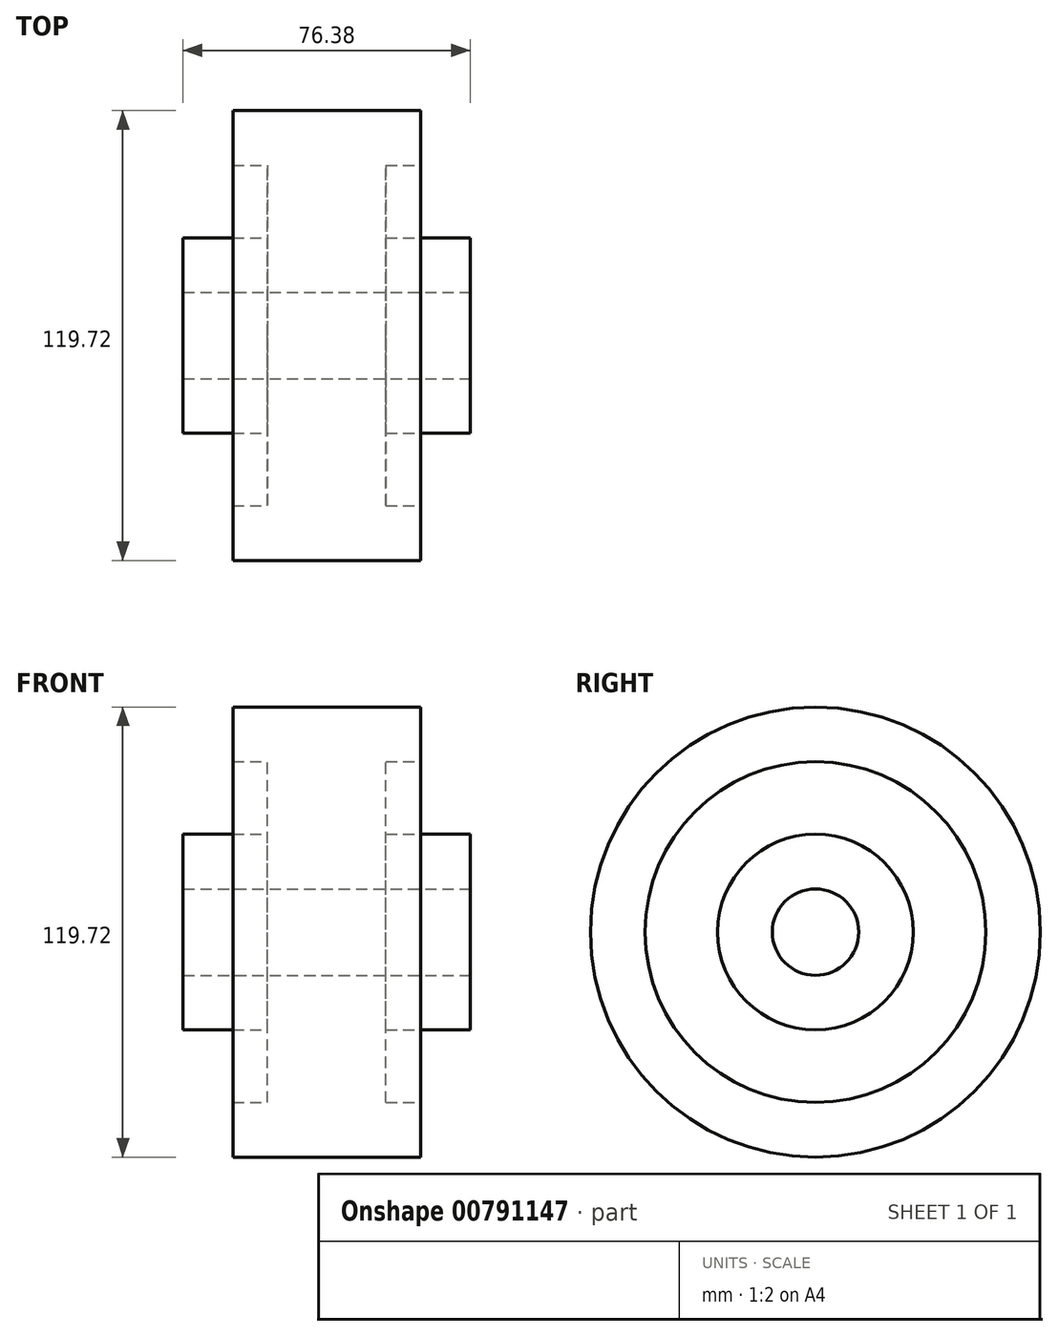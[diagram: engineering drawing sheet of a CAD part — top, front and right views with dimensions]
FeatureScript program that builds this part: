
annotation { "Feature Type Name" : "Feature", "Feature Type Description" : "" }
export const myFeature = defineFeature(function(context is Context, id is Id, definition is map)
    precondition{}
    {
        {
            var Q0;
            Q0=qCreatedBy(makeId("Front.planeOp"),FACE);
            var sketch = newSketch(context, id + "F0", { "sketchPlane" : qUnion([Q0])});
            skLineSegment(sketch, "E0", {"start": v(0, 0) * mm, "end": v(54.83, 0) * mm, "construction": true});
            skLineSegment(sketch, "E1", {"start": v(0, 11.5) * mm, "end": v(38.19, 11.5) * mm});
            skLineSegment(sketch, "E2", {"start": v(38.19, 11.5) * mm, "end": v(38.19, 26.03) * mm});
            skLineSegment(sketch, "E3", {"start": v(38.19, 26.03) * mm, "end": v(15.72, 26.03) * mm});
            skLineSegment(sketch, "E4", {"start": v(15.72, 26.03) * mm, "end": v(15.72, 45.32) * mm});
            skLineSegment(sketch, "E5", {"start": v(15.72, 45.32) * mm, "end": v(24.97, 45.32) * mm});
            skLineSegment(sketch, "E6", {"start": v(24.97, 45.32) * mm, "end": v(24.97, 59.86) * mm});
            skLineSegment(sketch, "E7", {"start": v(24.97, 59.86) * mm, "end": v(-24.97, 59.86) * mm});
            skLineSegment(sketch, "E8", {"start": v(-24.97, 59.86) * mm, "end": v(-24.97, 45.32) * mm});
            skLineSegment(sketch, "E9", {"start": v(-24.97, 45.32) * mm, "end": v(-15.72, 45.32) * mm});
            skLineSegment(sketch, "E10", {"start": v(-15.72, 45.32) * mm, "end": v(-15.72, 26.03) * mm});
            skLineSegment(sketch, "E11", {"start": v(-15.72, 26.03) * mm, "end": v(-38.19, 26.03) * mm});
            skLineSegment(sketch, "E12", {"start": v(-38.19, 26.03) * mm, "end": v(-38.19, 11.5) * mm});
            skLineSegment(sketch, "E13", {"start": v(-38.19, 11.5) * mm, "end": v(0, 11.5) * mm});
            skLineSegment(sketch, "E14", {"start": v(0, 0) * mm, "end": v(0, 67.25) * mm, "construction": true});
            skSolve(sketch);
        }
        {
            var Q0;
            Q0=sQuery(id+"F0.wireOp",EDGE,"E4");
            var Q1;
            Q1=sQuery(id+"F0.wireOp",EDGE,"E8");
            var Q2;
            Q2=sQuery(id+"F0.wireOp",EDGE,"E7");
            var Q3;
            Q3=sQuery(id+"F0.wireOp",EDGE,"E5");
            var Q4;
            Q4=sQuery(id+"F0.wireOp",EDGE,"E6");
            var Q5;
            Q5=sQuery(id+"F0.wireOp",EDGE,"E3");
            var Q6;
            Q6=sQuery(id+"F0.wireOp",EDGE,"E9");
            var Q7;
            Q7=sQuery(id+"F0.wireOp",EDGE,"E10");
            var Q8;
            Q8=sQuery(id+"F0.wireOp",EDGE,"E12");
            var Q9;
            Q9=sQuery(id+"F0.wireOp",EDGE,"E2");
            var Q10;
            Q10=sQuery(id+"F0.wireOp",EDGE,"E11");
            var Q11;
            Q11=sQuery(id+"F0.wireOp",EDGE,"E1");
            var Q12;
            Q12=sQuery(id+"F0.wireOp",EDGE,"E13");
            var Q13;
            Q13=sQuery(id+"F0.wireOp",EDGE,"E0");
            revolve(context, id + "F1", {"bodyType" : ToolBodyType.SURFACE, "surfaceOperationType" : NewSurfaceOperationType.NEW, "surfaceEntities" : qUnion([Q0, Q1, Q2, Q3, Q4, Q5, Q6, Q7, Q8, Q9, Q10, Q11, Q12]), "axis" : qUnion([Q13]), "revolveType" : RevolveType.FULL});
        }
    });
